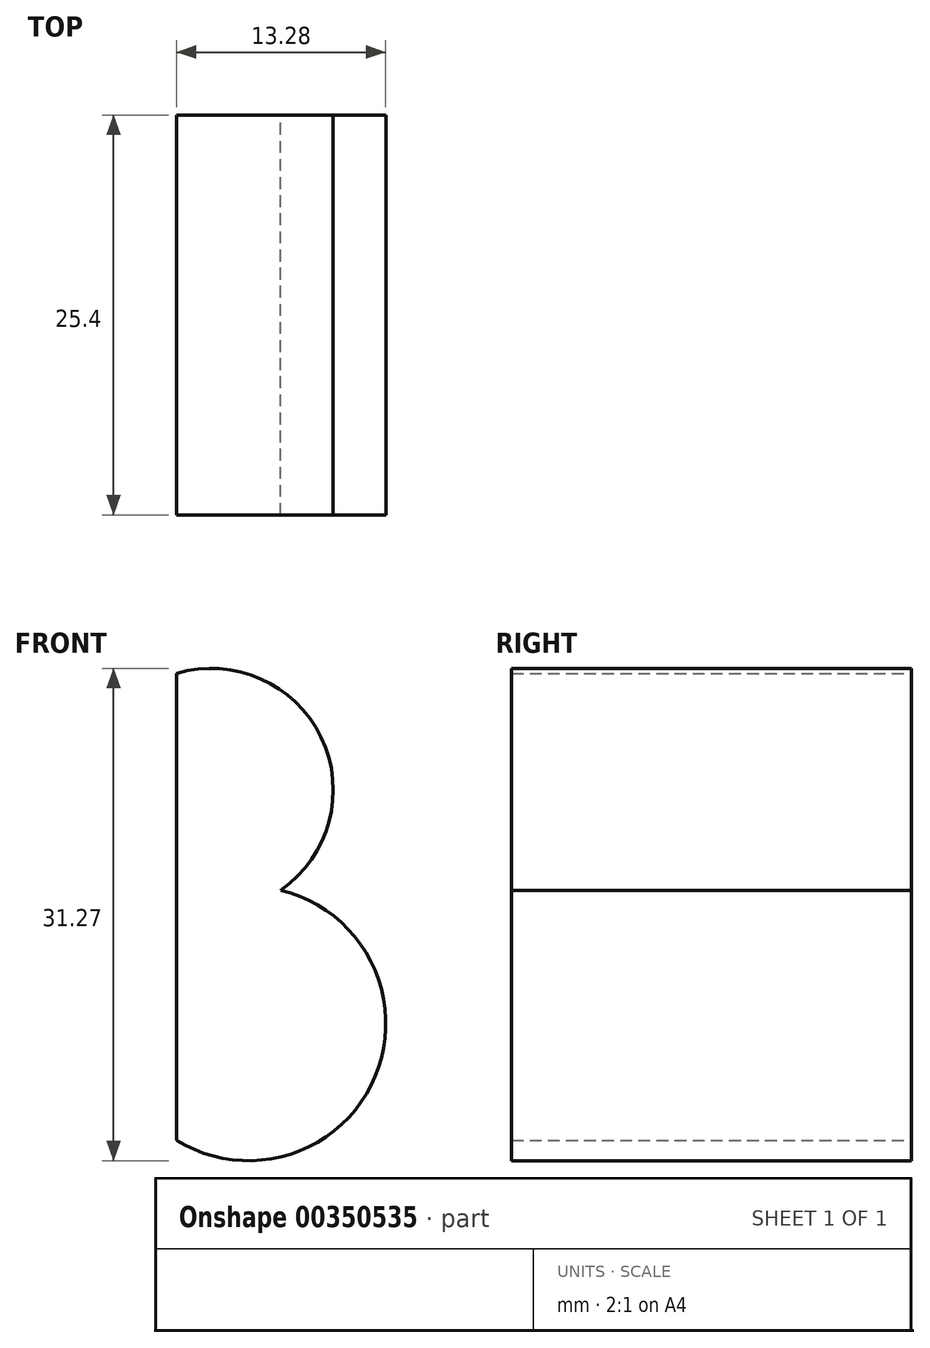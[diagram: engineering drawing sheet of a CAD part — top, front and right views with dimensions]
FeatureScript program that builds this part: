
annotation { "Feature Type Name" : "Feature", "Feature Type Description" : "" }
export const myFeature = defineFeature(function(context is Context, id is Id, definition is map)
    precondition{}
    {
        {
            var Q0;
            Q0=qCreatedBy(makeId("Front.planeOp"),FACE);
            var sketch = newSketch(context, id + "F0", { "sketchPlane" : qUnion([Q0])});
            skLineSegment(sketch, "E0", {"start": v(-67.98, 59.3) * mm, "end": v(-67.98, 29.65) * mm});
            skArc(sketch, "E1", {"start": v(-67.98, 44.48) * mm, "mid": v(-58.03, 51.9) * mm, "end": v(-67.98, 59.3) * mm});
            skArc(sketch, "E2", {"start": v(-67.98, 29.65) * mm, "mid": v(-54.7, 37.07) * mm, "end": v(-67.98, 44.48) * mm});
            skLineSegment(sketch, "E3", {"start": v(-47.28, 57.35) * mm, "end": v(-47.28, 29.1) * mm});
            skLineSegment(sketch, "E4", {"start": v(-47.28, 29.1) * mm, "end": v(-47.28, 57.35) * mm});
            skLineSegment(sketch, "E5", {"start": v(-33.85, 57.35) * mm, "end": v(-47.28, 57.35) * mm});
            skLineSegment(sketch, "E6", {"start": v(-47.28, 43.22) * mm, "end": v(-33.3, 43.22) * mm});
            skLineSegment(sketch, "E7", {"start": v(-33.3, 43.22) * mm, "end": v(-47.28, 43.22) * mm});
            skLineSegment(sketch, "E8", {"start": v(-47.28, 29.1) * mm, "end": v(-33.85, 29.1) * mm});
            skLineSegment(sketch, "E9", {"start": v(-33.85, 29.1) * mm, "end": v(-47.28, 29.1) * mm});
            skLineSegment(sketch, "E10", {"start": v(-19.86, 57.35) * mm, "end": v(-19.86, 29.1) * mm});
            skPoint(sketch, "E10.endSnap0", {"position": v(-40.56, 29.1) * mm});
            skLineSegment(sketch, "E11", {"start": v(-19.86, 29.1) * mm, "end": v(-19.86, 57.35) * mm});
            skLineSegment(sketch, "E12", {"start": v(-19.86, 57.35) * mm, "end": v(-4.48, 29.1) * mm});
            skLineSegment(sketch, "E13", {"start": v(-4.48, 29.1) * mm, "end": v(-4.48, 57.35) * mm});
            skLineSegment(sketch, "E14", {"start": v(-62.94, -21.26) * mm, "end": v(-62.94, -48.68) * mm});
            skLineSegment(sketch, "E15", {"start": v(-62.94, -48.68) * mm, "end": v(-62.94, -21.26) * mm});
            skLineSegment(sketch, "E16", {"start": v(-47.28, -21.26) * mm, "end": v(-62.94, -21.26) * mm});
            skLineSegment(sketch, "E17", {"start": v(-62.94, -34.97) * mm, "end": v(-47.28, -34.97) * mm});
            skLineSegment(sketch, "E18", {"start": v(-39.73, -21.26) * mm, "end": v(-39.73, -41.68) * mm});
            skLineSegment(sketch, "E19", {"start": v(-23.78, -21.26) * mm, "end": v(-23.78, -41.68) * mm});
            skArc(sketch, "E20", {"start": v(-39.73, -41.68) * mm, "mid": v(-31.75, -49.66) * mm, "end": v(-23.78, -41.68) * mm});
            skArc(sketch, "E21", {"start": v(-3.64, -20.42) * mm, "mid": v(-20.4, -34.69) * mm, "end": v(-3.64, -48.96) * mm});
            skLineSegment(sketch, "E22", {"start": v(4.76, -20.42) * mm, "end": v(4.76, -49.52) * mm});
            skLineSegment(sketch, "E23", {"start": v(4.76, -49.52) * mm, "end": v(4.76, -20.42) * mm});
            skLineSegment(sketch, "E24", {"start": v(4.76, -34.97) * mm, "end": v(14.27, -20.42) * mm});
            skLineSegment(sketch, "E25", {"start": v(14.27, -20.42) * mm, "end": v(4.76, -34.97) * mm});
            skLineSegment(sketch, "E26", {"start": v(4.76, -34.97) * mm, "end": v(17.34, -49.8) * mm});
            skLineSegment(sketch, "E27", {"start": v(34.97, -20.42) * mm, "end": v(34.97, -43.92) * mm});
            skLineSegment(sketch, "E28", {"start": v(34.97, -43.92) * mm, "end": v(34.97, -20.42) * mm});
            skLineSegment(sketch, "E29", {"start": v(51.47, -20.42) * mm, "end": v(51.47, -43.92) * mm});
            skArc(sketch, "E30", {"start": v(34.97, -43.92) * mm, "mid": v(43.22, -52.17) * mm, "end": v(51.47, -43.92) * mm});
            skSolve(sketch);
        }
        {
            var Q0;
            Q0 = qSketchRegion(id + "F0", true);
            extrude(context, id + "F1", {"entities" : qUnion([Q0]), "depth" : 25.4 * mm});
        }
        {
            var Q0;
            Q0 = qSketchRegion(id + "F0", true);
            extrude(context, id + "F2", {"entities" : qUnion([Q0]), "operationType" : NewBodyOperationType.ADD, "depth" : 25.4 * mm});
        }
    });
